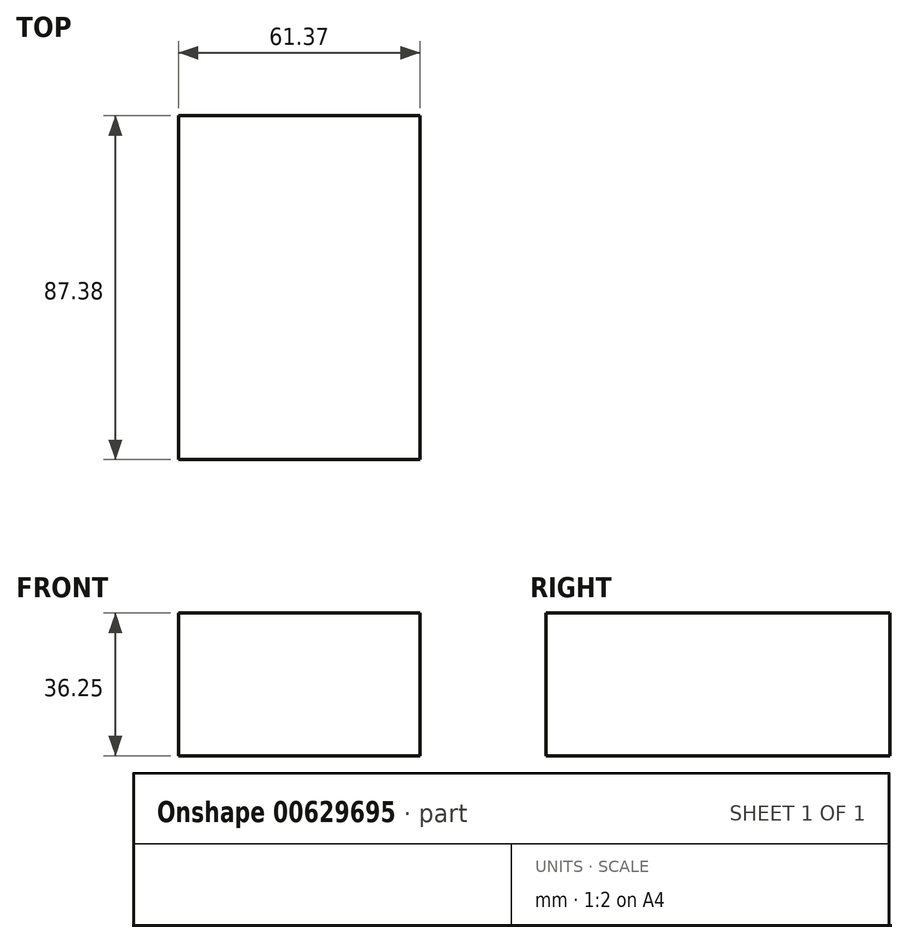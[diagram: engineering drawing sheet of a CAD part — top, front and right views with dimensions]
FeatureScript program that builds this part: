
annotation { "Feature Type Name" : "Feature", "Feature Type Description" : "" }
export const myFeature = defineFeature(function(context is Context, id is Id, definition is map)
    precondition{}
    {
        {
            var Q0;
            Q0=qCreatedBy(makeId("Front.planeOp"),FACE);
            var sketch = newSketch(context, id + "F0", { "sketchPlane" : qUnion([Q0])});
            skLineSegment(sketch, "E0.bottom", {"start": v(0, 0) * mm, "end": v(61.37, 0) * mm});
            skLineSegment(sketch, "E0.top", {"start": v(0, 36.25) * mm, "end": v(61.37, 36.25) * mm});
            skLineSegment(sketch, "E0.left", {"start": v(0, 0) * mm, "end": v(0, 36.25) * mm});
            skLineSegment(sketch, "E0.right", {"start": v(61.37, 0) * mm, "end": v(61.37, 36.25) * mm});
            skSolve(sketch);
        }
        {
            var Q0;
            Q0 = qSketchRegion(id + "F0", true);
            extrude(context, id + "F1", {"entities" : qUnion([Q0]), "depth" : 87.38 * mm, "offsetDistance" : 25.4 * mm});
        }
    });
